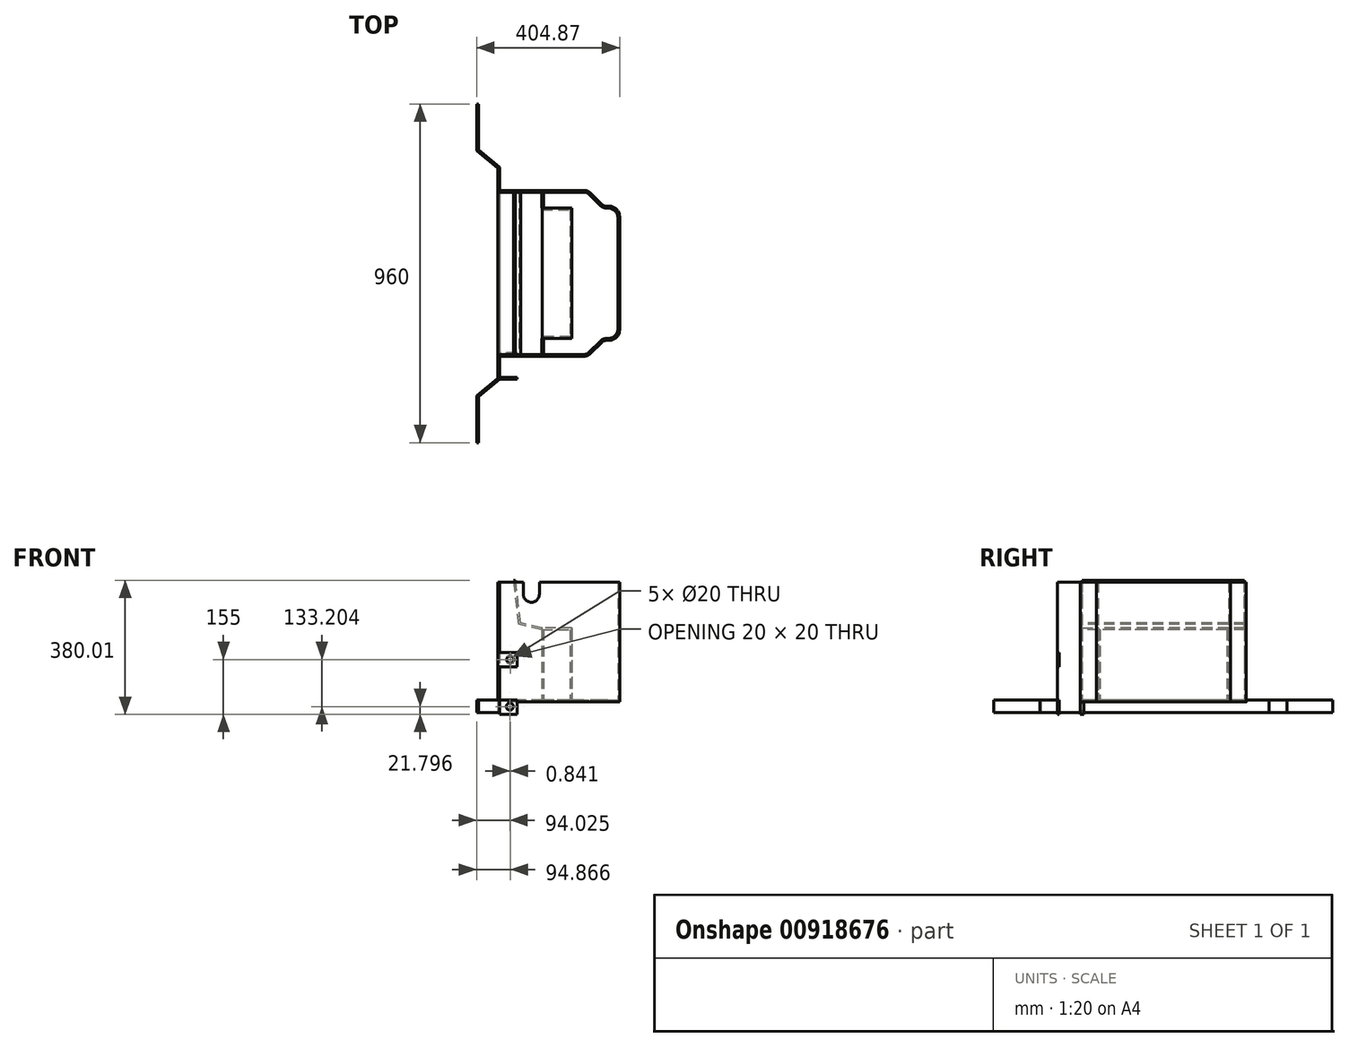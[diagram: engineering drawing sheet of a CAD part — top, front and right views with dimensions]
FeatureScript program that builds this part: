
annotation { "Feature Type Name" : "Feature", "Feature Type Description" : "" }
export const myFeature = defineFeature(function(context is Context, id is Id, definition is map)
    precondition{}
    {
        {
            var Q0;
            Q0=qCreatedBy(makeId("Front.planeOp"),FACE);
            var sketch = newSketch(context, id + "F0", { "sketchPlane" : qUnion([Q0])});
            skLineSegment(sketch, "E0", {"start": v(-514.8, 0) * mm, "end": v(635.2, 0) * mm, "construction": true});
            skLineSegment(sketch, "E1", {"start": v(-514.8, 0) * mm, "end": v(-514.8, 380) * mm, "construction": true});
            skCircle(sketch, "E2", {"center": v(-324.8, 190) * mm, "radius": 190 * mm, "construction": true});
            skPoint(sketch, "E2.first.point", {"position": v(-324.8, 0) * mm});
            skPoint(sketch, "E2.second.point", {"position": v(-514.8, 190) * mm});
            skPoint(sketch, "E2.third.point", {"position": v(-205.57, 337.94) * mm});
            skLineSegment(sketch, "E3", {"start": v(-514.8, 380) * mm, "end": v(635.2, 380) * mm, "construction": true});
            skLineSegment(sketch, "E4", {"start": v(635.2, 380) * mm, "end": v(635.2, 0) * mm, "construction": true});
            skCircle(sketch, "E5", {"center": v(445.2, 190) * mm, "radius": 190 * mm, "construction": true});
            skLineSegment(sketch, "E6", {"start": v(-134.8, 380) * mm, "end": v(-134.8, 0) * mm, "construction": true});
            skLineSegment(sketch, "E7", {"start": v(255.2, 380) * mm, "end": v(255.2, 0) * mm, "construction": true});
            skLineSegment(sketch, "E8", {"start": v(-542.2, 180) * mm, "end": v(670.63, 180) * mm, "construction": true});
            skLineSegment(sketch, "E9", {"start": v(-324.8, 408.83) * mm, "end": v(-324.8, -37.63) * mm, "construction": true});
            skLineSegment(sketch, "E10", {"start": v(445.2, 408.83) * mm, "end": v(445.2, -37.63) * mm, "construction": true});
            skLineSegment(sketch, "E11", {"start": v(294.65, 0) * mm, "end": v(294.65, 40) * mm, "construction": true});
            skLineSegment(sketch, "E12", {"start": v(294.65, 40) * mm, "end": v(635.2, 40) * mm, "construction": true});
            skSolve(sketch);
        }
        {
            var Q0;
            Q0=qCreatedBy(makeId("Top.planeOp"),FACE);
            var sketch = newSketch(context, id + "F1", { "sketchPlane" : qUnion([Q0])});
            skLineSegment(sketch, "E13", {"start": v(-514.8, 480) * mm, "end": v(-514.8, -480) * mm, "construction": true});
            skLineSegment(sketch, "E14", {"start": v(-134.8, 480) * mm, "end": v(-134.8, -480) * mm, "construction": true});
            skLineSegment(sketch, "E15", {"start": v(255.2, 480) * mm, "end": v(255.2, -480) * mm, "construction": true});
            skLineSegment(sketch, "E16", {"start": v(635.2, 480) * mm, "end": v(635.2, -480) * mm, "construction": true});
            skLineSegment(sketch, "E17", {"start": v(-514.8, 350) * mm, "end": v(125.2, 350) * mm, "construction": true});
            skLineSegment(sketch, "E18", {"start": v(-514.8, -350) * mm, "end": v(125.2, -350) * mm, "construction": true});
            skLineSegment(sketch, "E19", {"start": v(485.2, 180) * mm, "end": v(485.2, 0) * mm, "construction": true});
            skLineSegment(sketch, "E20", {"start": v(485.2, 0) * mm, "end": v(485.2, -180) * mm, "construction": true});
            skLineSegment(sketch, "E21", {"start": v(-514.8, 480) * mm, "end": v(635.2, 480) * mm, "construction": true});
            skLineSegment(sketch, "E22", {"start": v(-514.8, -480) * mm, "end": v(635.2, -480) * mm, "construction": true});
            skLineSegment(sketch, "E23", {"start": v(125.2, -350) * mm, "end": v(125.2, -350) * mm});
            skLineSegment(sketch, "E24", {"start": v(125.2, -350) * mm, "end": v(295.2, -350) * mm, "construction": true});
            skLineSegment(sketch, "E25", {"start": v(295.2, -350) * mm, "end": v(295.2, -235) * mm, "construction": true});
            skLineSegment(sketch, "E26", {"start": v(295.2, -235) * mm, "end": v(395.2, -235) * mm, "construction": true});
            skLineSegment(sketch, "E27", {"start": v(395.2, -235) * mm, "end": v(395.2, -180) * mm, "construction": true});
            skLineSegment(sketch, "E28", {"start": v(395.2, -180) * mm, "end": v(485.2, -180) * mm, "construction": true});
            skLineSegment(sketch, "E29", {"start": v(125.2, 350) * mm, "end": v(295.2, 350) * mm, "construction": true});
            skLineSegment(sketch, "E30.MirrorCS", {"start": v(125.2, 350) * mm, "end": v(125.2, 350) * mm});
            skLineSegment(sketch, "E31.MirrorCS", {"start": v(295.2, 350) * mm, "end": v(295.2, 235) * mm, "construction": true});
            skLineSegment(sketch, "E32.MirrorCS", {"start": v(295.2, 235) * mm, "end": v(395.2, 235) * mm, "construction": true});
            skLineSegment(sketch, "E33.MirrorCS", {"start": v(395.2, 235) * mm, "end": v(395.2, 180) * mm, "construction": true});
            skLineSegment(sketch, "E34.MirrorCS", {"start": v(395.2, 180) * mm, "end": v(485.2, 180) * mm, "construction": true});
            skLineSegment(sketch, "E35", {"start": v(295.2, 235) * mm, "end": v(295.2, -235) * mm, "construction": true});
            skSolve(sketch);
        }
        {
            var Q0;
            Q0=qCreatedBy(makeId("Front.planeOp"),FACE);
            var sketch = newSketch(context, id + "F2", { "sketchPlane" : qUnion([Q0])});
            skCircle(sketch, "E36", {"center": v(-214.8, 300) * mm, "radius": 300 * mm, "construction": true});
            skCircle(sketch, "E37", {"center": v(225.61, 60) * mm, "radius": 60 * mm, "construction": true});
            skLineSegment(sketch, "E38", {"start": v(225.61, 60) * mm, "end": v(485.39, 75) * mm, "construction": true});
            skLineSegment(sketch, "E39", {"start": v(485.39, 75) * mm, "end": v(485.39, 205.22) * mm, "construction": true});
            skLineSegment(sketch, "E40", {"start": v(485.39, 205.22) * mm, "end": v(333.21, 238.96) * mm, "construction": true});
            skLineSegment(sketch, "E41", {"start": v(333.21, 238.96) * mm, "end": v(289.28, 607.11) * mm, "construction": true});
            skLineSegment(sketch, "E42", {"start": v(289.28, 607.11) * mm, "end": v(240.41, 679.12) * mm, "construction": true});
            skLineSegment(sketch, "E43", {"start": v(240.41, 679.12) * mm, "end": v(-524.68, 643.12) * mm, "construction": true});
            skLineSegment(sketch, "E44", {"start": v(-219.79, 35) * mm, "end": v(-139.8, 35) * mm, "construction": true});
            skLineSegment(sketch, "E45", {"start": v(-179.8, 64.67) * mm, "end": v(-179.8, 16.9) * mm, "construction": true});
            skPoint(sketch, "E45.startSnap0", {"position": v(-179.8, 35) * mm});
            skLineSegment(sketch, "E46", {"start": v(-214.8, 300) * mm, "end": v(-214.8, 0) * mm, "construction": true});
            skLineSegment(sketch, "E47", {"start": v(-524.68, 643.12) * mm, "end": v(-510.83, 348.64) * mm});
            skSolve(sketch);
        }
        {
            var Q0;
            Q0=qCreatedBy(makeId("Top.planeOp"),FACE);
            var sketch = newSketch(context, id + "F3", { "sketchPlane" : qUnion([Q0])});
            skLineSegment(sketch, "E48", {"start": v(-514.8, 350) * mm, "end": v(135.2, 350) * mm, "construction": true});
            skLineSegment(sketch, "E49", {"start": v(-514.8, -350) * mm, "end": v(135.2, -350) * mm, "construction": true});
            skLineSegment(sketch, "E50", {"start": v(485.2, 180) * mm, "end": v(485.2, 0) * mm, "construction": true});
            skLineSegment(sketch, "E51", {"start": v(485.2, 0) * mm, "end": v(485.2, -180) * mm, "construction": true});
            skLineSegment(sketch, "E52", {"start": v(135.2, -350) * mm, "end": v(485.2, -284.96) * mm, "construction": true});
            skLineSegment(sketch, "E53", {"start": v(485.2, -284.96) * mm, "end": v(485.2, -180) * mm, "construction": true});
            skLineSegment(sketch, "E54", {"start": v(485.2, 180) * mm, "end": v(485.2, 284.96) * mm, "construction": true});
            skLineSegment(sketch, "E55", {"start": v(485.2, 284.96) * mm, "end": v(135.2, 350) * mm, "construction": true});
            skLineSegment(sketch, "E56", {"start": v(-514.8, 350) * mm, "end": v(-514.8, -350) * mm, "construction": true});
            skSolve(sketch);
        }
        {
            var Q0;
            Q0=qCreatedBy(makeId("Top.planeOp"),FACE);
            var sketch = newSketch(context, id + "F4", { "sketchPlane" : qUnion([Q0])});
            skLineSegment(sketch, "E57", {"start": v(125.2, 350) * mm, "end": v(125.2, 350) * mm});
            skLineSegment(sketch, "E58", {"start": v(295.2, 300) * mm, "end": v(295.2, -300) * mm});
            skLineSegment(sketch, "E59", {"start": v(235.2, -350) * mm, "end": v(-514.8, -350) * mm});
            skLineSegment(sketch, "E60", {"start": v(-514.8, -350) * mm, "end": v(-514.8, 350) * mm});
            skLineSegment(sketch, "E61", {"start": v(-514.8, 150) * mm, "end": v(-414.8, 150) * mm});
            skLineSegment(sketch, "E62", {"start": v(-414.8, 150) * mm, "end": v(-414.8, -150) * mm});
            skLineSegment(sketch, "E63", {"start": v(-414.8, -150) * mm, "end": v(-514.8, -150) * mm});
            skLineSegment(sketch, "E64.left", {"start": v(-359.6, 150) * mm, "end": v(-359.6, -150) * mm});
            skLineSegment(sketch, "E65.bottom", {"start": v(-94.94, 150) * mm, "end": v(93.6, 150) * mm});
            skLineSegment(sketch, "E65.top", {"start": v(-94.94, -150) * mm, "end": v(93.6, -150) * mm});
            skLineSegment(sketch, "E65.left", {"start": v(-94.94, 150) * mm, "end": v(-94.94, -150) * mm});
            skLineSegment(sketch, "E65.right", {"start": v(93.6, 150) * mm, "end": v(93.6, -150) * mm});
            skLineSegment(sketch, "E66.left", {"start": v(295.2, 235) * mm, "end": v(295.2, -235) * mm});
            skLineSegment(sketch, "E67", {"start": v(-514.8, 350) * mm, "end": v(235.2, 350) * mm});
            skLineSegment(sketch, "E68", {"start": v(-212.1, 152.43) * mm, "end": v(-212.1, -147.57) * mm});
            skLineSegment(sketch, "E69", {"start": v(-212.1, -147.57) * mm, "end": v(-359.6, -150) * mm});
            skLineSegment(sketch, "E70", {"start": v(-212.1, 152.43) * mm, "end": v(-359.6, 150) * mm});
            skPoint(sketch, "E71.orphan", {"position": v(295.2, 350) * mm});
            skLineSegment(sketch, "E72", {"start": v(235.2, 350) * mm, "end": v(295.2, 300) * mm});
            skLineSegment(sketch, "E73", {"start": v(295.2, -300) * mm, "end": v(235.2, -350) * mm});
            skSolve(sketch);
        }
        {
            var Q0;
            {var subQ6=sQuery(id+"F4.wireOp",EDGE,"E59");Q0=makeQuery(id+"F4.imprint","IMPRINT",FACE,{"disambiguationData":[TD([[makeQuery(id+"F4.imprint","IMPRINT",EDGE,{"derivedFrom":subQ6}),-1.0]])]});}
            var sketch = newSketch(context, id + "F5", { "sketchPlane" : qUnion([Q0])});
            skLineSegment(sketch, "E74.bottom", {"start": v(295.2, 235) * mm, "end": v(536.05, 235) * mm});
            skLineSegment(sketch, "E74.top", {"start": v(295.2, -235) * mm, "end": v(536.05, -235) * mm});
            skLineSegment(sketch, "E74.left", {"start": v(295.2, 235) * mm, "end": v(295.2, -235) * mm});
            skLineSegment(sketch, "E74.right", {"start": v(635.2, 160) * mm, "end": v(635.2, -160) * mm});
            skLineSegment(sketch, "E75", {"start": v(550.04, -229.3) * mm, "end": v(584.38, -195.7) * mm});
            skLineSegment(sketch, "E76", {"start": v(598.36, -190) * mm, "end": v(605.2, -190) * mm});
            skLineSegment(sketch, "E77", {"start": v(550.04, 229.3) * mm, "end": v(584.38, 195.7) * mm});
            skLineSegment(sketch, "E78", {"start": v(598.36, 190) * mm, "end": v(605.2, 190) * mm});
            skPoint(sketch, "E79.orphan", {"position": v(635.2, 235) * mm});
            skPoint(sketch, "E80.orphan", {"position": v(635.2, -235) * mm});
            skPoint(sketch, "E81.visualSharp", {"position": v(590.2, -190) * mm});
            skArc(sketch, "E81.filletArc", {"start": v(598.36, -190) * mm, "mid": v(590.8, -191.48) * mm, "end": v(584.38, -195.7) * mm});
            skPoint(sketch, "E82.visualSharp", {"position": v(544.2, -235) * mm});
            skArc(sketch, "E82.filletArc", {"start": v(536.05, -235) * mm, "mid": v(543.6, -233.52) * mm, "end": v(550.04, -229.3) * mm});
            skPoint(sketch, "E83.visualSharp", {"position": v(590.2, 190) * mm});
            skArc(sketch, "E83.filletArc", {"start": v(584.38, 195.7) * mm, "mid": v(590.8, 191.48) * mm, "end": v(598.36, 190) * mm});
            skPoint(sketch, "E84.visualSharp", {"position": v(544.2, 235) * mm});
            skArc(sketch, "E84.filletArc", {"start": v(550.04, 229.3) * mm, "mid": v(543.6, 233.52) * mm, "end": v(536.05, 235) * mm});
            skPoint(sketch, "E85.visualSharp", {"position": v(635.2, 190) * mm});
            skArc(sketch, "E85.filletArc", {"start": v(635.2, 160) * mm, "mid": v(626.42, 181.21) * mm, "end": v(605.2, 190) * mm});
            skPoint(sketch, "E86.visualSharp", {"position": v(635.2, -190) * mm});
            skArc(sketch, "E86.filletArc", {"start": v(605.2, -190) * mm, "mid": v(626.42, -181.21) * mm, "end": v(635.2, -160) * mm});
            skSolve(sketch);
        }
        {
            var Q0;
            Q0=makeQuery(id+"F4.imprint","IMPRINT",FACE,{"disambiguationData":[TD([[makeQuery(id+"F4.imprint","IMPRINT",EDGE,{"derivedFrom":sQuery(id+"F4.wireOp",EDGE,"E65.bottom")}),-1.0]])]});
            var sketch = newSketch(context, id + "F6", { "sketchPlane" : qUnion([Q0])});
            skLineSegment(sketch, "E87", {"start": v(235.34, 480) * mm, "end": v(235.34, 350) * mm});
            skLineSegment(sketch, "E88", {"start": v(295.2, 300) * mm, "end": v(295.2, -300) * mm});
            skLineSegment(sketch, "E89.1", {"start": v(230.34, 480) * mm, "end": v(230.34, 347.66) * mm});
            skLineSegment(sketch, "E89.3", {"start": v(290.2, 297.66) * mm, "end": v(290.2, -297.66) * mm});
            skLineSegment(sketch, "E90", {"start": v(230.34, 480) * mm, "end": v(235.34, 480) * mm});
            skLineSegment(sketch, "E91", {"start": v(230.34, -480) * mm, "end": v(235.34, -480) * mm});
            skLineSegment(sketch, "E92", {"start": v(235.34, -350) * mm, "end": v(235.34, -480) * mm});
            skLineSegment(sketch, "E93", {"start": v(230.34, -480) * mm, "end": v(230.34, -347.66) * mm});
            skLineSegment(sketch, "E94", {"start": v(295.2, -300) * mm, "end": v(235.34, -350) * mm});
            skLineSegment(sketch, "E95", {"start": v(230.34, -347.66) * mm, "end": v(290.2, -297.66) * mm});
            skPoint(sketch, "E96.orphan", {"position": v(230.34, -297.66) * mm});
            skPoint(sketch, "E97.orphan", {"position": v(235.34, -301.2) * mm});
            skLineSegment(sketch, "E98", {"start": v(295.2, 300) * mm, "end": v(235.34, 350) * mm});
            skLineSegment(sketch, "E99", {"start": v(230.34, 347.66) * mm, "end": v(290.2, 297.66) * mm});
            skPoint(sketch, "E100.orphan", {"position": v(235.34, 298.8) * mm});
            skPoint(sketch, "E101.orphan", {"position": v(290.2, 295) * mm});
            skSolve(sketch);
        }
        {
            var Q0;
            Q0=qSketchRegion(id+"F5",true);
            extrude(context, id + "F7", {"entities" : qUnion([Q0]), "depth" : 40 * mm, "offsetDistance" : 25.4 * mm, "hasSecondDirection" : true, "secondDirectionOppositeDirection" : false, "secondDirectionDepth" : 35 * mm});
        }
        {
            var Q0;
            Q0=qSketchRegion(id+"F6",true);
            extrude(context, id + "F8", {"entities" : qUnion([Q0]), "depth" : 40 * mm, "offsetDistance" : 25.4 * mm, "hasSecondDirection" : true, "secondDirectionOppositeDirection" : false, "secondDirectionDepth" : 5 * mm});
        }
        {
            var Q0;
            Q0=makeQuery(id+"F7.opExtrude","CAP_FACE",FACE,{"disambiguationData":[OSD([sQuery(id+"F5.wireOp",EDGE,"E74.bottom"),sQuery(id+"F5.wireOp",EDGE,"E74.top"),sQuery(id+"F5.wireOp",EDGE,"E74.left"),sQuery(id+"F5.wireOp",EDGE,"E74.right")])],"isStart":false});
            var sketch = newSketch(context, id + "F9", { "sketchPlane" : qUnion([Q0])});
            skPoint(sketch, "E102.trimOffspring.end.orphan", {"position": v(635.2, -145) * mm});
            skPoint(sketch, "E103.orphan", {"position": v(587.86, -195) * mm});
            skPoint(sketch, "E104.start.orphan", {"position": v(585.92, -190) * mm});
            skPoint(sketch, "E105.end.orphan", {"position": v(536.63, -235) * mm});
            skPoint(sketch, "E106.start.orphan", {"position": v(635.2, 190) * mm});
            skPoint(sketch, "E107.end.orphan", {"position": v(587.86, 190) * mm});
            skPoint(sketch, "E107.start.orphan", {"position": v(536.63, 234.74) * mm});
            skLineSegment(sketch, "E108", {"start": v(295.2, 235) * mm, "end": v(536.05, 235) * mm});
            skLineSegment(sketch, "E109", {"start": v(550.04, 229.3) * mm, "end": v(584.38, 195.7) * mm});
            skLineSegment(sketch, "E110", {"start": v(598.36, 190) * mm, "end": v(605.2, 190) * mm});
            skLineSegment(sketch, "E111", {"start": v(635.2, 160) * mm, "end": v(635.2, -160) * mm});
            skLineSegment(sketch, "E112", {"start": v(605.2, -190) * mm, "end": v(598.36, -190) * mm});
            skLineSegment(sketch, "E113", {"start": v(584.38, -195.7) * mm, "end": v(550.04, -229.3) * mm});
            skLineSegment(sketch, "E114", {"start": v(536.05, -235) * mm, "end": v(295.2, -235) * mm});
            skLineSegment(sketch, "E115.0", {"start": v(534.01, -230) * mm, "end": v(295.2, -230) * mm});
            skLineSegment(sketch, "E115.1", {"start": v(582.34, -190.7) * mm, "end": v(548, -224.3) * mm});
            skLineSegment(sketch, "E115.2", {"start": v(602.2, -185) * mm, "end": v(596.32, -185) * mm});
            skLineSegment(sketch, "E115.3", {"start": v(295.2, 230) * mm, "end": v(534.01, 230) * mm});
            skLineSegment(sketch, "E115.4", {"start": v(548, 224.3) * mm, "end": v(582.34, 190.7) * mm});
            skLineSegment(sketch, "E115.5", {"start": v(596.32, 185) * mm, "end": v(602.2, 185) * mm});
            skLineSegment(sketch, "E115.6", {"start": v(630.2, 157) * mm, "end": v(630.2, -157) * mm});
            skLineSegment(sketch, "E116", {"start": v(295.2, 235) * mm, "end": v(295.2, 230) * mm});
            skLineSegment(sketch, "E117", {"start": v(295.2, -230) * mm, "end": v(295.2, -235) * mm});
            skPoint(sketch, "E118.visualSharp", {"position": v(544.2, 235) * mm});
            skArc(sketch, "E118.filletArc", {"start": v(550.04, 229.3) * mm, "mid": v(543.6, 233.52) * mm, "end": v(536.05, 235) * mm});
            skPoint(sketch, "E119.visualSharp", {"position": v(542.17, 230) * mm});
            skArc(sketch, "E119.filletArc", {"start": v(548, 224.3) * mm, "mid": v(541.56, 228.52) * mm, "end": v(534.01, 230) * mm});
            skPoint(sketch, "E120.visualSharp", {"position": v(590.2, 190) * mm});
            skArc(sketch, "E120.filletArc", {"start": v(584.38, 195.7) * mm, "mid": v(590.8, 191.48) * mm, "end": v(598.36, 190) * mm});
            skPoint(sketch, "E121.visualSharp", {"position": v(588.17, 185) * mm});
            skArc(sketch, "E121.filletArc", {"start": v(582.34, 190.7) * mm, "mid": v(588.77, 186.48) * mm, "end": v(596.32, 185) * mm});
            skPoint(sketch, "E122.visualSharp", {"position": v(544.2, -235) * mm});
            skArc(sketch, "E122.filletArc", {"start": v(536.05, -235) * mm, "mid": v(543.6, -233.52) * mm, "end": v(550.04, -229.3) * mm});
            skPoint(sketch, "E123.visualSharp", {"position": v(542.17, -230) * mm});
            skArc(sketch, "E123.filletArc", {"start": v(534.01, -230) * mm, "mid": v(541.56, -228.52) * mm, "end": v(548, -224.3) * mm});
            skPoint(sketch, "E124.visualSharp", {"position": v(590.2, -190) * mm});
            skArc(sketch, "E124.filletArc", {"start": v(598.36, -190) * mm, "mid": v(590.8, -191.48) * mm, "end": v(584.38, -195.7) * mm});
            skPoint(sketch, "E125.visualSharp", {"position": v(588.17, -185) * mm});
            skArc(sketch, "E125.filletArc", {"start": v(596.32, -185) * mm, "mid": v(588.77, -186.48) * mm, "end": v(582.34, -190.7) * mm});
            skPoint(sketch, "E126.visualSharp", {"position": v(635.2, -190) * mm});
            skArc(sketch, "E126.filletArc", {"start": v(605.2, -190) * mm, "mid": v(626.42, -181.21) * mm, "end": v(635.2, -160) * mm});
            skArc(sketch, "E127.filletArc", {"start": v(635.2, 160) * mm, "mid": v(626.42, 181.21) * mm, "end": v(605.2, 190) * mm});
            skPoint(sketch, "E128.end.orphan", {"position": v(630.2, 190) * mm});
            skPoint(sketch, "E129.visualSharp", {"position": v(630.2, -185) * mm});
            skArc(sketch, "E129.filletArc", {"start": v(602.2, -185) * mm, "mid": v(622, -176.8) * mm, "end": v(630.2, -157) * mm});
            skPoint(sketch, "E130.visualSharp", {"position": v(630.2, 185) * mm});
            skArc(sketch, "E130.filletArc", {"start": v(630.2, 157) * mm, "mid": v(622, 176.8) * mm, "end": v(602.2, 185) * mm});
            skSolve(sketch);
        }
        {
            var Q0;
            Q0=makeQuery(id+"F7.opExtrude","CAP_FACE",FACE,{"disambiguationData":[OSD([sQuery(id+"F5.wireOp",EDGE,"E74.bottom"),sQuery(id+"F5.wireOp",EDGE,"E74.top"),sQuery(id+"F5.wireOp",EDGE,"E74.left"),sQuery(id+"F5.wireOp",EDGE,"E74.right")])],"isStart":false});
            var sketch = newSketch(context, id + "F10", { "sketchPlane" : qUnion([Q0])});
            skLineSegment(sketch, "E131", {"start": v(415.2, 230) * mm, "end": v(415.2, 179.76) * mm});
            skLineSegment(sketch, "E132", {"start": v(415.2, 179.76) * mm, "end": v(495.2, 179.76) * mm});
            skLineSegment(sketch, "E133", {"start": v(495.2, 179.76) * mm, "end": v(495.2, -180) * mm});
            skLineSegment(sketch, "E134", {"start": v(495.2, -180) * mm, "end": v(415.2, -180) * mm});
            skLineSegment(sketch, "E135", {"start": v(415.2, -180) * mm, "end": v(415.2, -230) * mm});
            skLineSegment(sketch, "E136.0", {"start": v(420.2, -185) * mm, "end": v(420.2, -230) * mm});
            skLineSegment(sketch, "E136.1", {"start": v(420.2, 230) * mm, "end": v(420.2, 184.76) * mm});
            skLineSegment(sketch, "E136.2", {"start": v(420.2, 184.76) * mm, "end": v(500.2, 184.76) * mm});
            skLineSegment(sketch, "E136.3", {"start": v(500.2, 184.76) * mm, "end": v(500.2, -185) * mm});
            skLineSegment(sketch, "E136.4", {"start": v(500.2, -185) * mm, "end": v(420.2, -185) * mm});
            skLineSegment(sketch, "E137", {"start": v(415.2, 230) * mm, "end": v(420.2, 230) * mm});
            skLineSegment(sketch, "E138", {"start": v(415.2, -230) * mm, "end": v(420.2, -230) * mm});
            skSolve(sketch);
        }
        {
            var Q0;
            Q0=makeQuery(id+"F10.imprint","IMPRINT",FACE,{"disambiguationData":[TD([[makeQuery(id+"F10.imprint","IMPRINT",EDGE,{"derivedFrom":sQuery(id+"F10.wireOp",EDGE,"E131")}),1.0]])]});
            extrude(context, id + "F11", {"entities" : qUnion([Q0]), "operationType" : NewBodyOperationType.ADD, "depth" : 200 * mm, "offsetDistance" : 25 * mm});
        }
        {
            var Q0;
            Q0=makeQuery(id+"F11.opExtrude","SWEPT_FACE",FACE,{"disambiguationData":[OSD([sQuery(id+"F10.wireOp",EDGE,"E136.4")])]});
            var sketch = newSketch(context, id + "F12", { "sketchPlane" : qUnion([Q0])});
            skLineSegment(sketch, "E139", {"start": v(500.2, 240) * mm, "end": v(415.08, 240) * mm});
            skLineSegment(sketch, "E140", {"start": v(415.08, 240) * mm, "end": v(350.22, 255.05) * mm});
            skLineSegment(sketch, "E141", {"start": v(350.22, 255.05) * mm, "end": v(335.23, 380.01) * mm});
            skLineSegment(sketch, "E142.0", {"start": v(354.76, 259.13) * mm, "end": v(340.26, 380.01) * mm});
            skLineSegment(sketch, "E142.1", {"start": v(415.65, 245) * mm, "end": v(354.76, 259.13) * mm});
            skLineSegment(sketch, "E142.2", {"start": v(500.2, 245) * mm, "end": v(415.65, 245) * mm});
            skLineSegment(sketch, "E143", {"start": v(500.2, 240) * mm, "end": v(500.2, 245) * mm});
            skLineSegment(sketch, "E144", {"start": v(335.23, 380.01) * mm, "end": v(340.26, 380.01) * mm});
            skSolve(sketch);
        }
        {
            var Q0;
            Q0=qSketchRegion(id+"F12",true);
            extrude(context, id + "F13", {"entities" : qUnion([Q0]), "oppositeDirection" : true, "depth" : 369.76 * mm, "offsetDistance" : 25 * mm});
        }
        {
            var Q0;
            Q0=makeQuery(id+"F13.opExtrude","CAP_FACE",FACE,{"disambiguationData":[OSD([sQuery(id+"F12.wireOp",EDGE,"E139"),sQuery(id+"F12.wireOp",EDGE,"E140"),sQuery(id+"F12.wireOp",EDGE,"E141"),sQuery(id+"F12.wireOp",EDGE,"E142.0"),sQuery(id+"F12.wireOp",EDGE,"E142.1"),sQuery(id+"F12.wireOp",EDGE,"E142.2"),sQuery(id+"F12.wireOp",EDGE,"GDHxoDt4-68R8-k933-4VTx-wFCzrUYWveIz"),sQuery(id+"F12.wireOp",EDGE,"E143")])],"isStart":true});
            var sketch = newSketch(context, id + "F14", { "sketchPlane" : qUnion([Q0])});
            skLineSegment(sketch, "E145", {"start": v(350.22, 255.05) * mm, "end": v(354.76, 259.13) * mm});
            skLineSegment(sketch, "E146", {"start": v(354.76, 259.13) * mm, "end": v(354.76, 259.13) * mm});
            skLineSegment(sketch, "E147", {"start": v(354.76, 259.13) * mm, "end": v(415.08, 245.13) * mm});
            skLineSegment(sketch, "E148", {"start": v(415.08, 240) * mm, "end": v(350.22, 255.05) * mm});
            skLineSegment(sketch, "E149", {"start": v(350.22, 255.05) * mm, "end": v(350.22, 255.05) * mm});
            skLineSegment(sketch, "E150", {"start": v(415.08, 245.13) * mm, "end": v(415.08, 240) * mm});
            skSolve(sketch);
        }
        {
            var Q0;
            Q0=makeQuery(id+"F14.imprint","IMPRINT",FACE,{"disambiguationData":[TD([[makeQuery(id+"F14.imprint","IMPRINT",EDGE,{"derivedFrom":sQuery(id+"F14.wireOp",EDGE,"E145")}),-1.0]])]});
            extrude(context, id + "F15", {"entities" : qUnion([Q0]), "operationType" : NewBodyOperationType.ADD, "depth" : 45 * mm, "offsetDistance" : 25 * mm});
        }
        {
            var Q0;
            Q0=makeQuery(id+"F13.opExtrude","CAP_FACE",FACE,{"disambiguationData":[OSD([sQuery(id+"F12.wireOp",EDGE,"E139"),sQuery(id+"F12.wireOp",EDGE,"E140"),sQuery(id+"F12.wireOp",EDGE,"E141"),sQuery(id+"F12.wireOp",EDGE,"E142.0"),sQuery(id+"F12.wireOp",EDGE,"E142.1"),sQuery(id+"F12.wireOp",EDGE,"E142.2"),sQuery(id+"F12.wireOp",EDGE,"GDHxoDt4-68R8-k933-4VTx-wFCzrUYWveIz"),sQuery(id+"F12.wireOp",EDGE,"E143")])],"isStart":false});
            var sketch = newSketch(context, id + "F16", { "sketchPlane" : qUnion([Q0])});
            skLineSegment(sketch, "E151", {"start": v(-415.08, 240) * mm, "end": v(-415.08, 245.13) * mm});
            skLineSegment(sketch, "E152", {"start": v(-415.08, 245.13) * mm, "end": v(-354.76, 259.13) * mm});
            skLineSegment(sketch, "E153", {"start": v(-354.76, 259.13) * mm, "end": v(-354.76, 259.13) * mm});
            skLineSegment(sketch, "E154", {"start": v(-354.76, 259.13) * mm, "end": v(-350.22, 255.05) * mm});
            skLineSegment(sketch, "E155", {"start": v(-350.22, 255.05) * mm, "end": v(-350.22, 255.05) * mm});
            skLineSegment(sketch, "E156", {"start": v(-350.22, 255.05) * mm, "end": v(-415.08, 240) * mm});
            skSolve(sketch);
        }
        {
            var Q0;
            Q0=qSketchRegion(id+"F16",true);
            extrude(context, id + "F17", {"entities" : qUnion([Q0]), "operationType" : NewBodyOperationType.ADD, "depth" : 45 * mm, "offsetDistance" : 25 * mm});
        }
        {
            var Q0;
            {var subQ0=sQuery(id+"F12.wireOp",EDGE,"E142.1");var subQ1=sQuery(id+"F12.wireOp",EDGE,"E142.0");var subQ2=sQuery(id+"F12.wireOp",EDGE,"E141");var subQ3=sQuery(id+"F12.wireOp",EDGE,"E140");var subQ4=sQuery(id+"F12.wireOp",EDGE,"E144");Q0=makeQuery(id+"F15.boolean.opBoolean","SPLIT",FACE,{"disambiguationData":[TD([makeQuery(id+"F13.opExtrude","SWEPT_FACE",FACE,{"disambiguationData":[OSD([subQ2])]})])],"derivedFrom":makeQuery(id+"F13.opExtrude","CAP_FACE",FACE,{"disambiguationData":[OSD([sQuery(id+"F12.wireOp",EDGE,"E139"),subQ3,subQ2,subQ1,subQ0,sQuery(id+"F12.wireOp",EDGE,"E142.2"),sQuery(id+"F12.wireOp",EDGE,"E143"),subQ4])],"isStart":true})});}
            extrude(context, id + "F18", {"entities" : qUnion([Q0]), "operationType" : NewBodyOperationType.ADD, "depth" : 45 * mm, "offsetDistance" : 25 * mm});
        }
        {
            var Q0;
            {var subQ0=sQuery(id+"F12.wireOp",EDGE,"E142.1");var subQ1=sQuery(id+"F12.wireOp",EDGE,"E142.0");var subQ2=sQuery(id+"F12.wireOp",EDGE,"E141");var subQ3=sQuery(id+"F12.wireOp",EDGE,"E140");var subQ4=sQuery(id+"F12.wireOp",EDGE,"E144");Q0=makeQuery(id+"F17.boolean.opBoolean","SPLIT",FACE,{"disambiguationData":[TD([makeQuery(id+"F13.opExtrude","SWEPT_FACE",FACE,{"disambiguationData":[OSD([subQ2])]})])],"derivedFrom":makeQuery(id+"F13.opExtrude","CAP_FACE",FACE,{"disambiguationData":[OSD([sQuery(id+"F12.wireOp",EDGE,"E139"),subQ3,subQ2,subQ1,subQ0,sQuery(id+"F12.wireOp",EDGE,"E142.2"),sQuery(id+"F12.wireOp",EDGE,"E143"),subQ4])],"isStart":false})});}
            extrude(context, id + "F19", {"entities" : qUnion([Q0]), "operationType" : NewBodyOperationType.ADD, "depth" : 45 * mm, "offsetDistance" : 25 * mm});
        }
        {
            var Q0;
            Q0=qSketchRegion(id+"F9",true);
            extrude(context, id + "F20", {"entities" : qUnion([Q0]), "operationType" : NewBodyOperationType.ADD, "depth" : 335 * mm, "offsetDistance" : 25 * mm});
        }
        {
            var Q0;
            Q0=makeQuery(id+"F20.boolean.opBoolean","MERGE",FACE,{"derivedFrom":[makeQuery(id+"F7.opExtrude","SWEPT_FACE",FACE,{"disambiguationData":[OSD([sQuery(id+"F5.wireOp",EDGE,"E74.top")])]}),makeQuery(id+"F20.opExtrude","SWEPT_FACE",FACE,{"disambiguationData":[OSD([sQuery(id+"F9.wireOp",EDGE,"E114")])]})]});
            var sketch = newSketch(context, id + "F21", { "sketchPlane" : qUnion([Q0])});
            skLineSegment(sketch, "E157.bottom", {"start": v(530.05, 35) * mm, "end": v(510.05, 35) * mm});
            skLineSegment(sketch, "E157.top", {"start": v(530.05, 65) * mm, "end": v(510.05, 65) * mm});
            skLineSegment(sketch, "E157.left", {"start": v(530.05, 35) * mm, "end": v(530.05, 65) * mm});
            skLineSegment(sketch, "E157.right", {"start": v(510.05, 35) * mm, "end": v(510.05, 65) * mm});
            skLineSegment(sketch, "E158.bottom", {"start": v(530.05, 218) * mm, "end": v(510.05, 218) * mm});
            skLineSegment(sketch, "E158.top", {"start": v(530.05, 248) * mm, "end": v(510.05, 248) * mm});
            skLineSegment(sketch, "E158.left", {"start": v(530.05, 218) * mm, "end": v(530.05, 248) * mm});
            skLineSegment(sketch, "E158.right", {"start": v(510.05, 218) * mm, "end": v(510.05, 248) * mm});
            skLineSegment(sketch, "E159.bottom", {"start": v(388.15, 218) * mm, "end": v(368.15, 218) * mm});
            skLineSegment(sketch, "E159.top", {"start": v(388.15, 248) * mm, "end": v(368.15, 248) * mm});
            skLineSegment(sketch, "E159.left", {"start": v(388.15, 218) * mm, "end": v(388.15, 248) * mm});
            skLineSegment(sketch, "E159.right", {"start": v(368.15, 218) * mm, "end": v(368.15, 248) * mm});
            skLineSegment(sketch, "E160.bottom", {"start": v(388.15, 35) * mm, "end": v(368.15, 35) * mm});
            skLineSegment(sketch, "E160.top", {"start": v(388.15, 65) * mm, "end": v(368.15, 65) * mm});
            skLineSegment(sketch, "E160.left", {"start": v(388.15, 35) * mm, "end": v(388.15, 65) * mm});
            skLineSegment(sketch, "E160.right", {"start": v(368.15, 35) * mm, "end": v(368.15, 65) * mm});
            skSolve(sketch);
        }
        {
            var Q0;
            Q0=makeQuery(id+"F7.opExtrude","CAP_FACE",FACE,{"disambiguationData":[OSD([sQuery(id+"F5.wireOp",EDGE,"E74.bottom"),sQuery(id+"F5.wireOp",EDGE,"E74.top"),sQuery(id+"F5.wireOp",EDGE,"E74.left"),sQuery(id+"F5.wireOp",EDGE,"E74.right"),sQuery(id+"F5.wireOp",EDGE,"E75"),sQuery(id+"F5.wireOp",EDGE,"E76"),sQuery(id+"F5.wireOp",EDGE,"E77"),sQuery(id+"F5.wireOp",EDGE,"E78"),sQuery(id+"F5.wireOp",EDGE,"E81.filletArc"),sQuery(id+"F5.wireOp",EDGE,"E82.filletArc"),sQuery(id+"F5.wireOp",EDGE,"E83.filletArc"),sQuery(id+"F5.wireOp",EDGE,"E84.filletArc"),sQuery(id+"F5.wireOp",EDGE,"E85.filletArc"),sQuery(id+"F5.wireOp",EDGE,"E86.filletArc")])],"isStart":true});
            var sketch = newSketch(context, id + "F22", { "sketchPlane" : qUnion([Q0])});
            skLineSegment(sketch, "E161", {"start": v(295.2, 235) * mm, "end": v(345.36, 235) * mm});
            skLineSegment(sketch, "E162", {"start": v(345.36, 235) * mm, "end": v(345.36, 225) * mm});
            skLineSegment(sketch, "E163", {"start": v(345.36, 225) * mm, "end": v(295.2, 225) * mm});
            skLineSegment(sketch, "E164", {"start": v(295.2, 225) * mm, "end": v(295.2, 235) * mm});
            skSolve(sketch);
        }
        {
            var Q0;
            Q0=qSketchRegion(id+"F22",true);
            extrude(context, id + "F23", {"entities" : qUnion([Q0]), "operationType" : NewBodyOperationType.ADD, "depth" : 35 * mm, "offsetDistance" : 25 * mm});
        }
        {
            var Q0;
            {var subQ9=sQuery(id+"F6.wireOp",EDGE,"E88");var subQ12=sQuery(id+"F5.wireOp",EDGE,"E74.top");Q0=makeQuery(id+"F23.boolean.opBoolean","SPLIT",FACE,{"disambiguationData":[TD([makeQuery(id+"F7.opExtrude","SWEPT_FACE",FACE,{"disambiguationData":[OSD([subQ12])]})])],"derivedFrom":makeQuery(id+"F8.opExtrude","SWEPT_FACE",FACE,{"disambiguationData":[OSD([subQ9])]})});}
            var sketch = newSketch(context, id + "F24", { "sketchPlane" : qUnion([Q0])});
            skLineSegment(sketch, "E165.bottom", {"start": v(-300, 40) * mm, "end": v(-295, 40) * mm});
            skLineSegment(sketch, "E165.top", {"start": v(-300, 0) * mm, "end": v(-295, 0) * mm});
            skLineSegment(sketch, "E165.left", {"start": v(-300, 40) * mm, "end": v(-300, 0) * mm});
            skLineSegment(sketch, "E165.right", {"start": v(-295, 40) * mm, "end": v(-295, 0) * mm});
            skSolve(sketch);
        }
        {
            var Q0;
            {var subQ0=sQuery(id+"F24.wireOp",EDGE,"E165.bottom");Q0=makeQuery(id+"F24.imprint","IMPRINT",FACE,{"disambiguationData":[TD([[makeQuery(id+"F24.imprint","IMPRINT",EDGE,{"derivedFrom":subQ0}),1.0]])]});}
            var Q1;
            {var subQ0=sQuery(id+"F24.wireOp",EDGE,"E165.top");Q1=makeQuery(id+"F24.imprint","IMPRINT",FACE,{"disambiguationData":[TD([[makeQuery(id+"F24.imprint","IMPRINT",EDGE,{"derivedFrom":subQ0}),1.0]])]});}
            extrude(context, id + "F25", {"entities" : qUnion([Q0, Q1]), "operationType" : NewBodyOperationType.ADD, "depth" : 50 * mm, "offsetDistance" : 25 * mm});
        }
        {
            var Q0;
            Q0=makeQuery(id+"F23.opExtrude","SWEPT_FACE",FACE,{"disambiguationData":[OSD([sQuery(id+"F22.wireOp",EDGE,"E163")])]});
            var sketch = newSketch(context, id + "F26", { "sketchPlane" : qUnion([Q0])});
            skCircle(sketch, "E166", {"center": v(-324.37, 21.8) * mm, "radius": 10 * mm});
            skSolve(sketch);
        }
        {
            var Q0;
            Q0=makeQuery(id+"F26.imprint","IMPRINT",FACE,{"disambiguationData":[TD([[makeQuery(id+"F26.imprint","IMPRINT",EDGE,{"derivedFrom":sQuery(id+"F26.wireOp",EDGE,"E166")}),1.0]])]});
            extrude(context, id + "F27", {"entities" : qUnion([Q0]), "operationType" : NewBodyOperationType.REMOVE, "endBound" : BoundingType.THROUGH_ALL, "oppositeDirection" : true, "depth" : 25 * mm, "offsetDistance" : 25 * mm});
        }
        {
            var Q0;
            Q0=makeQuery(id+"F25.boolean.opBoolean","MERGE",FACE,{"derivedFrom":[makeQuery(id+"F20.boolean.opBoolean","MERGE",FACE,{"disambiguationData":[OD(1.0)],"derivedFrom":[makeQuery(id+"F8.opExtrude","CAP_FACE",FACE,{"disambiguationData":[OSD([sQuery(id+"F6.wireOp",EDGE,"E87"),sQuery(id+"F6.wireOp",EDGE,"kXhIhEsm-VaYh-IsTm-mEO1-Klr7QDPccnhX"),sQuery(id+"F6.wireOp",EDGE,"E88"),sQuery(id+"F6.wireOp",EDGE,"7ZgBzFFx-wRTC-32i4-HmPx-MqD1xixbeFq9"),sQuery(id+"F6.wireOp",EDGE,"fKfhEorN-Rs1V-oMIc-bA7I-jXg4C3z7bY3x"),sQuery(id+"F6.wireOp",EDGE,"E89.0"),sQuery(id+"F6.wireOp",EDGE,"E89.1"),sQuery(id+"F6.wireOp",EDGE,"E89.2"),sQuery(id+"F6.wireOp",EDGE,"E89.3"),sQuery(id+"F6.wireOp",EDGE,"E89.4"),sQuery(id+"F6.wireOp",EDGE,"E90"),sQuery(id+"F6.wireOp",EDGE,"E91")])],"isStart":false}),makeQuery(id+"F7.opExtrude","CAP_FACE",FACE,{"disambiguationData":[OSD([sQuery(id+"F5.wireOp",EDGE,"E74.bottom"),sQuery(id+"F5.wireOp",EDGE,"E74.top"),sQuery(id+"F5.wireOp",EDGE,"E74.left"),sQuery(id+"F5.wireOp",EDGE,"E74.right"),sQuery(id+"F5.wireOp",EDGE,"E75"),sQuery(id+"F5.wireOp",EDGE,"E76"),sQuery(id+"F5.wireOp",EDGE,"E77"),sQuery(id+"F5.wireOp",EDGE,"E78"),sQuery(id+"F5.wireOp",EDGE,"E81.filletArc"),sQuery(id+"F5.wireOp",EDGE,"E82.filletArc"),sQuery(id+"F5.wireOp",EDGE,"E83.filletArc"),sQuery(id+"F5.wireOp",EDGE,"E84.filletArc"),sQuery(id+"F5.wireOp",EDGE,"E85.filletArc"),sQuery(id+"F5.wireOp",EDGE,"E86.filletArc")])],"isStart":false})]}),makeQuery(id+"F25.opExtrude","SWEPT_FACE",FACE,{"disambiguationData":[OSD([sQuery(id+"F24.wireOp",EDGE,"E165.bottom")])]})]});
            var sketch = newSketch(context, id + "F28", { "sketchPlane" : qUnion([Q0])});
            skLineSegment(sketch, "E167.bottom", {"start": v(295.2, -230) * mm, "end": v(290.2, -230) * mm});
            skLineSegment(sketch, "E167.top", {"start": v(295.2, -300) * mm, "end": v(290.2, -300) * mm});
            skLineSegment(sketch, "E167.left", {"start": v(295.2, -230) * mm, "end": v(295.2, -300) * mm});
            skLineSegment(sketch, "E167.right", {"start": v(290.2, -230) * mm, "end": v(290.2, -300) * mm});
            skSolve(sketch);
        }
        {
            var Q0;
            {var subQ2=sQuery(id+"F28.wireOp",EDGE,"E167.bottom");Q0=makeQuery(id+"F28.imprint","IMPRINT",FACE,{"disambiguationData":[TD([[makeQuery(id+"F28.imprint","IMPRINT",EDGE,{"derivedFrom":subQ2}),1.0]])]});}
            extrude(context, id + "F29", {"entities" : qUnion([Q0]), "operationType" : NewBodyOperationType.ADD, "depth" : 335 * mm, "offsetDistance" : 25 * mm});
        }
        {
            var Q0;
            {var subQ3=sQuery(id+"F24.wireOp",EDGE,"E165.left");var subQ7=sQuery(id+"F5.wireOp",EDGE,"E74.top");var subQ18=sQuery(id+"F6.wireOp",EDGE,"E88");var subQ24=makeQuery(id+"F7.opExtrude","SWEPT_FACE",FACE,{"disambiguationData":[OSD([subQ7])]});var subQ27=makeQuery(id+"F23.boolean.opBoolean","SPLIT",FACE,{"disambiguationData":[TD([subQ24])],"derivedFrom":makeQuery(id+"F8.opExtrude","SWEPT_FACE",FACE,{"disambiguationData":[OSD([subQ18])]})});Q0=makeQuery(id+"F29.boolean.opBoolean","MERGE",FACE,{"derivedFrom":[makeQuery(id+"F25.boolean.opBoolean","SPLIT",FACE,{"disambiguationData":[TD([makeQuery(id+"F25.opExtrude","SWEPT_FACE",FACE,{"disambiguationData":[OSD([subQ3])]})])],"derivedFrom":subQ27}),makeQuery(id+"F25.boolean.opBoolean","SPLIT",FACE,{"disambiguationData":[TD([subQ24])],"derivedFrom":subQ27}),makeQuery(id+"F29.opExtrude","SWEPT_FACE",FACE,{"disambiguationData":[OSD([sQuery(id+"F28.wireOp",EDGE,"E167.left")])]})]});}
            var sketch = newSketch(context, id + "F30", { "sketchPlane" : qUnion([Q0])});
            skLineSegment(sketch, "E168.bottom", {"start": v(-300, 175) * mm, "end": v(-295, 175) * mm});
            skLineSegment(sketch, "E168.top", {"start": v(-300, 135) * mm, "end": v(-295, 135) * mm});
            skLineSegment(sketch, "E168.left", {"start": v(-300, 175) * mm, "end": v(-300, 135) * mm});
            skLineSegment(sketch, "E168.right", {"start": v(-295, 175) * mm, "end": v(-295, 135) * mm});
            skSolve(sketch);
        }
        {
            var Q0;
            Q0=makeQuery(id+"F30.imprint","IMPRINT",FACE,{"disambiguationData":[TD([[makeQuery(id+"F30.imprint","IMPRINT",EDGE,{"derivedFrom":sQuery(id+"F30.wireOp",EDGE,"E168.bottom")}),-1.0]])]});
            extrude(context, id + "F31", {"entities" : qUnion([Q0]), "operationType" : NewBodyOperationType.ADD, "depth" : 50 * mm, "offsetDistance" : 25 * mm});
        }
        {
            var Q0;
            Q0=makeQuery(id+"F31.opExtrude","SWEPT_FACE",FACE,{"disambiguationData":[OSD([sQuery(id+"F30.wireOp",EDGE,"E168.left")])]});
            var sketch = newSketch(context, id + "F32", { "sketchPlane" : qUnion([Q0])});
            skCircle(sketch, "E169", {"center": v(325.2, 155) * mm, "radius": 10 * mm});
            skPoint(sketch, "E169.centerSnap0", {"position": v(325.2, 175) * mm});
            skPoint(sketch, "E169.centerSnap1", {"position": v(345.2, 155) * mm});
            skSolve(sketch);
        }
        {
            var Q0;
            Q0=makeQuery(id+"F32.imprint","IMPRINT",FACE,{"disambiguationData":[TD([[makeQuery(id+"F32.imprint","IMPRINT",EDGE,{"derivedFrom":sQuery(id+"F32.wireOp",EDGE,"E169")}),1.0]])]});
            extrude(context, id + "F33", {"entities" : qUnion([Q0]), "operationType" : NewBodyOperationType.REMOVE, "endBound" : BoundingType.THROUGH_ALL, "oppositeDirection" : true, "depth" : 25 * mm, "offsetDistance" : 25 * mm});
        }
        {
            var Q0;
            Q0=makeQuery(id+"F21.imprint","IMPRINT",FACE,{"disambiguationData":[TD([[makeQuery(id+"F21.imprint","IMPRINT",EDGE,{"derivedFrom":sQuery(id+"F21.wireOp",EDGE,"E157.top")}),-1.0]])]});
            var sketch = newSketch(context, id + "F34", { "sketchPlane" : qUnion([Q0])});
            skArc(sketch, "E170", {"start": v(362.7, 340) * mm, "mid": v(385.2, 317.5) * mm, "end": v(407.7, 340) * mm});
            skLineSegment(sketch, "E171", {"start": v(362.7, 340) * mm, "end": v(362.7, 375.37) * mm});
            skLineSegment(sketch, "E172", {"start": v(362.7, 375.37) * mm, "end": v(407.7, 375.37) * mm});
            skLineSegment(sketch, "E173", {"start": v(407.7, 375.37) * mm, "end": v(407.7, 340) * mm});
            skSolve(sketch);
        }
        {
            var Q0;
            {var subQ0=sQuery(id+"F34.wireOp",EDGE,"E170");Q0=makeQuery(id+"F34.imprint","IMPRINT",FACE,{"disambiguationData":[TD([[makeQuery(id+"F34.imprint","IMPRINT",EDGE,{"derivedFrom":subQ0}),1.0]])]});}
            extrude(context, id + "F35", {"entities" : qUnion([Q0]), "operationType" : NewBodyOperationType.REMOVE, "endBound" : BoundingType.THROUGH_ALL, "oppositeDirection" : true, "depth" : 25 * mm, "offsetDistance" : 25 * mm});
        }
    });
